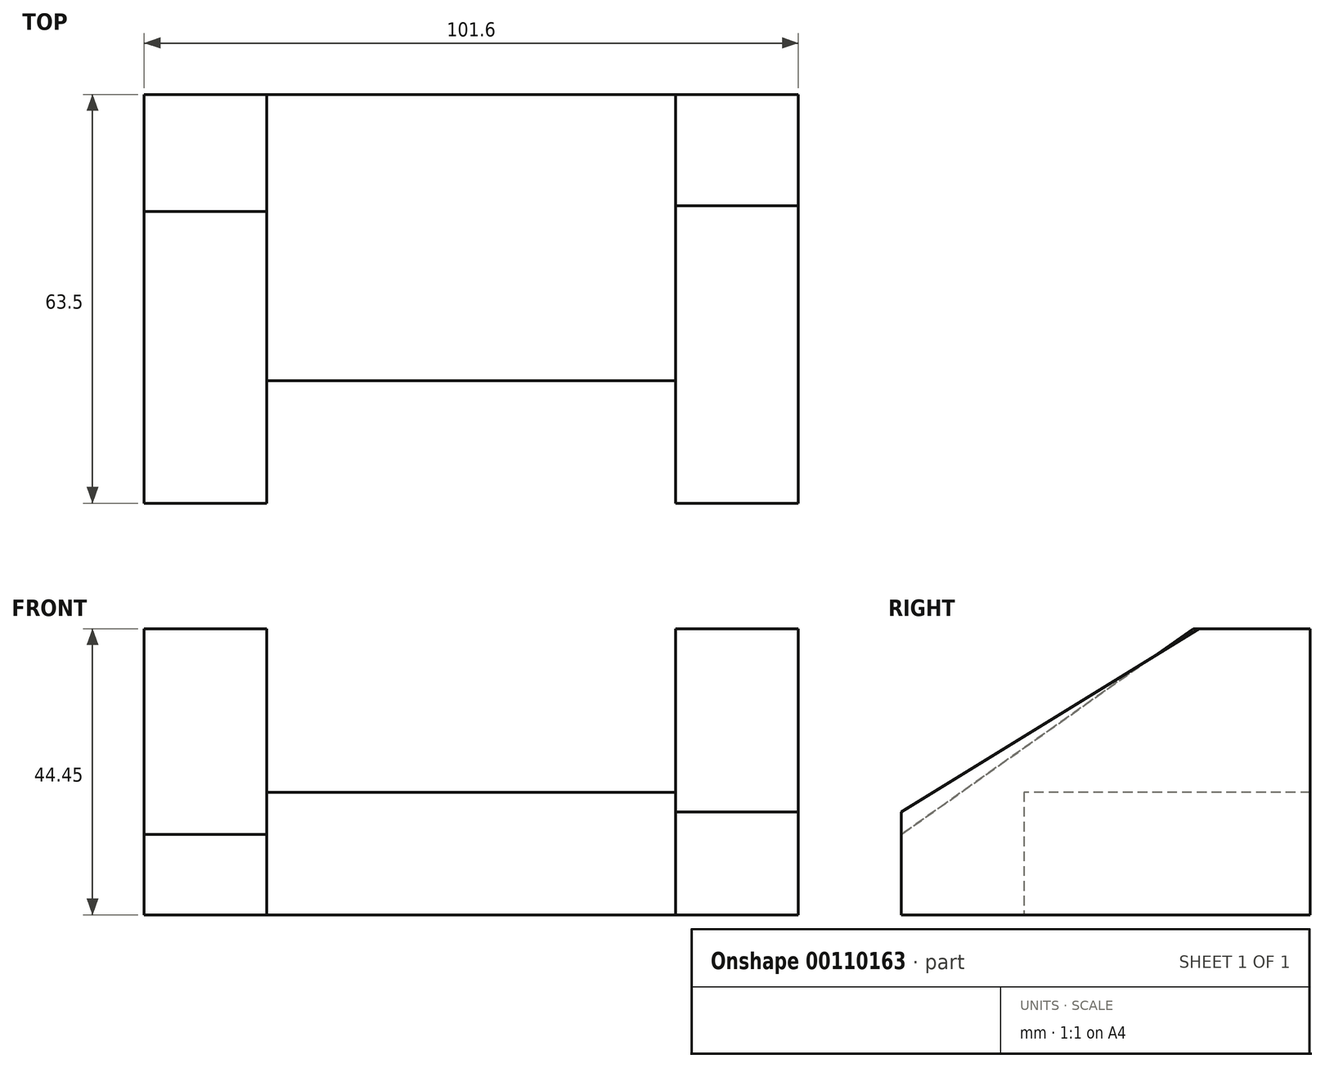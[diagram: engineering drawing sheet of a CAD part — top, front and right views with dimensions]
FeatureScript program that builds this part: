
annotation { "Feature Type Name" : "Feature", "Feature Type Description" : "" }
export const myFeature = defineFeature(function(context is Context, id is Id, definition is map)
    precondition{}
    {
        {
            var Q0;
            Q0=qCreatedBy(makeId("Top.planeOp"),FACE);
            var sketch = newSketch(context, id + "F0", { "sketchPlane" : qUnion([Q0])});
            skPoint(sketch, "E0.middle", {"position": v(0, 0) * mm});
            skLineSegment(sketch, "E1.bottom", {"start": v(29.6, 27.68) * mm, "end": v(-33.9, 27.68) * mm});
            skLineSegment(sketch, "E1.top", {"start": v(29.6, -16.77) * mm, "end": v(-33.9, -16.77) * mm});
            skLineSegment(sketch, "E1.left", {"start": v(29.6, 27.68) * mm, "end": v(29.6, -16.77) * mm});
            skLineSegment(sketch, "E1.right", {"start": v(-33.9, 27.68) * mm, "end": v(-33.9, -16.77) * mm});
            skLineSegment(sketch, "E2.bottom", {"start": v(-33.9, 27.68) * mm, "end": v(-52.95, 27.68) * mm});
            skLineSegment(sketch, "E2.top", {"start": v(-33.9, -35.82) * mm, "end": v(-52.95, -35.82) * mm});
            skLineSegment(sketch, "E2.left", {"start": v(-33.9, 27.68) * mm, "end": v(-33.9, -35.82) * mm});
            skLineSegment(sketch, "E2.right", {"start": v(-52.95, 27.68) * mm, "end": v(-52.95, -35.82) * mm});
            skLineSegment(sketch, "E3.bottom", {"start": v(29.6, 27.68) * mm, "end": v(48.65, 27.68) * mm});
            skLineSegment(sketch, "E3.top", {"start": v(29.6, -35.82) * mm, "end": v(48.65, -35.82) * mm});
            skLineSegment(sketch, "E3.left", {"start": v(29.6, 27.68) * mm, "end": v(29.6, -35.82) * mm});
            skLineSegment(sketch, "E3.right", {"start": v(48.65, 27.68) * mm, "end": v(48.65, -35.82) * mm});
            skSolve(sketch);
        }
        {
            var Q0;
            {var subQ3=sQuery(id+"F0.wireOp",EDGE,"E3.bottom");Q0=makeQuery(id+"F0.imprint","IMPRINT",FACE,{"disambiguationData":[TD([[makeQuery(id+"F0.imprint","IMPRINT",EDGE,{"derivedFrom":subQ3}),-1.0]])]});}
            var Q1;
            {var subQ3=sQuery(id+"F0.wireOp",EDGE,"E2.bottom");Q1=makeQuery(id+"F0.imprint","IMPRINT",FACE,{"disambiguationData":[TD([[makeQuery(id+"F0.imprint","IMPRINT",EDGE,{"derivedFrom":subQ3}),1.0]])]});}
            extrude(context, id + "F1", {"entities" : qUnion([Q0, Q1]), "depth" : 44.45 * mm});
        }
        {
            var Q0;
            {var subQ0=sQuery(id+"F0.wireOp",EDGE,"E1.bottom");Q0=makeQuery(id+"F0.imprint","IMPRINT",FACE,{"disambiguationData":[TD([[makeQuery(id+"F0.imprint","IMPRINT",EDGE,{"derivedFrom":subQ0}),1.0]])]});}
            extrude(context, id + "F2", {"entities" : qUnion([Q0]), "depth" : 19.05 * mm});
        }
        {
            var Q0;
            Q0=makeQuery(id+"F1.opExtrude","SWEPT_FACE",FACE,{"disambiguationData":[OSD([sQuery(id+"F0.wireOp",EDGE,"E2.right")])]});
            var sketch = newSketch(context, id + "F3", { "sketchPlane" : qUnion([Q0])});
            skLineSegment(sketch, "E4", {"start": v(35.82, 12.48) * mm, "end": v(-9.48, 44.45) * mm});
            skLineSegment(sketch, "E5", {"start": v(-68.98, 6.12) * mm, "end": v(-114.27, 38.09) * mm});
            skSolve(sketch);
        }
        {
            var Q0;
            Q0 = qSketchRegion(id + "F3", true);
            var Q1;
            {var subQ0=sQuery(id+"F3.wireOp",EDGE,"E4");Q1=makeQuery(id+"F3.imprint","IMPRINT",FACE,{"disambiguationData":[TD([[makeQuery(id+"F3.imprint","IMPRINT",EDGE,{"derivedFrom":subQ0}),-1.0]])]});}
            extrude(context, id + "F4", {"entities" : qUnion([Q0, Q1]), "operationType" : NewBodyOperationType.REMOVE, "oppositeDirection" : true, "depth" : 25.4 * mm});
        }
        {
            var Q0;
            Q0=makeQuery(id+"F1.opExtrude","SWEPT_FACE",FACE,{"disambiguationData":[OSD([sQuery(id+"F0.wireOp",EDGE,"E3.right")])]});
            var sketch = newSketch(context, id + "F5", { "sketchPlane" : qUnion([Q0])});
            skLineSegment(sketch, "E6", {"start": v(-35.82, 16) * mm, "end": v(10.38, 44.45) * mm});
            skSolve(sketch);
        }
        {
            var Q0;
            {var subQ0=sQuery(id+"F5.wireOp",EDGE,"E6");Q0=makeQuery(id+"F5.imprint","IMPRINT",FACE,{"disambiguationData":[TD([[makeQuery(id+"F5.imprint","IMPRINT",EDGE,{"derivedFrom":subQ0}),1.0]])]});}
            extrude(context, id + "F6", {"entities" : qUnion([Q0]), "operationType" : NewBodyOperationType.REMOVE, "oppositeDirection" : true, "depth" : 25.4 * mm});
        }
    });
